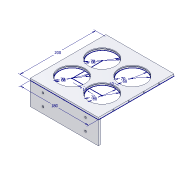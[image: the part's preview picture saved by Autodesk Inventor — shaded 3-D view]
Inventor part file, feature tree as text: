
AUTODESK INVENTOR PART (.ipt)
format: ipt  version: 2020.3 (Build 243373010, 373A)  size: 168,960 bytes
history: native  units: mm
features: sketch x4, extrude x3, hole x2
ambient origin geometry x8: Origin, YZ Plane, XZ Plane, XY Plane, X Axis, Y Axis, Z Axis, Center Point
bodies: Solid1 (feature_tree)
feature tree (9):
  sketch  "Sketch1"  dims[d0=180.0mm d1=200.0mm]
  extrude  "Extrusion1"  Depth=200.0mm
  extrude  "Extrusion2"  Depth=70.0mm
  hole  "Hole1"  [1 undecoded]
  extrude  "Extrusion3"  Depth=5.0mm TaperAngle=0.0deg
  hole  "Hole2"  [1 undecoded]
  sketch  "Sketch2"  dims[d2=70.0mm d3=70.0mm]
  sketch  "Sketch3"  dims[d4=70.0mm d5=70.0mm d6=10.0mm]
  sketch  "Sketch4"  dims[d7=10.0mm d9=5.0mm d10=0.0mm d11=68.0mm d12=68.0mm d13=68.0mm d14=68.0mm d15=3.0mm d16=0.0mm d18=2.0mm d19=2.0mm d20=2.0mm d21=2.0mm d23=40.0mm d24=40.0mm d25=40.0mm d26=40.0mm d28=3.242mm d29=8.0mm d30=3.708mm d31=2.0mm d32=14.3117mm d33=11.8mm d34=0.0mm d35=6.0mm d36=60.0mm d37=0.0mm d38=4.917mm d39=12.0mm d40=3.708mm d41=2.0mm d42=14.3117mm d43=17.1mm d44=0.0mm d45=2.5mm]
note: 2 required parameter values undecoded (feature->parameter linkage not recoverable at this tier; creation-order binding heuristic only, values carry confidence <= 0.55)
